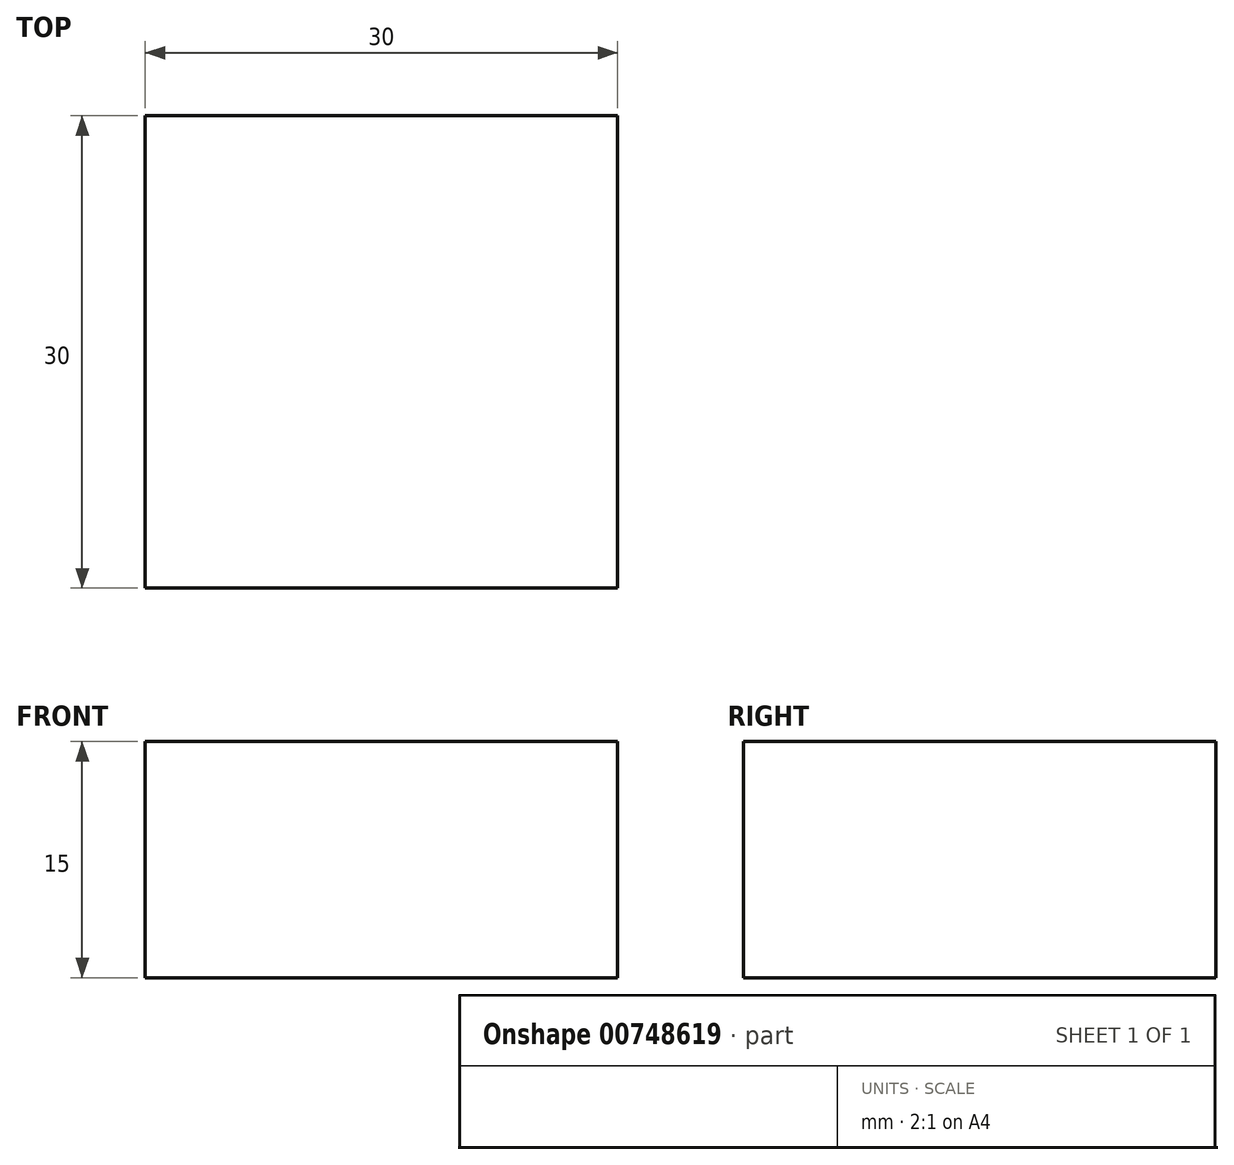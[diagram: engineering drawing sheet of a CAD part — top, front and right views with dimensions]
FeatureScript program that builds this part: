
annotation { "Feature Type Name" : "Feature", "Feature Type Description" : "" }
export const myFeature = defineFeature(function(context is Context, id is Id, definition is map)
    precondition{}
    {
        {
            var Q0;
            Q0=qCreatedBy(makeId("Top.planeOp"),FACE);
            var sketch = newSketch(context, id + "F0", { "sketchPlane" : qUnion([Q0])});
            skLineSegment(sketch, "E0.bottom", {"start": v(-15, -15) * mm, "end": v(15, -15) * mm});
            skLineSegment(sketch, "E0.top", {"start": v(-15, 15) * mm, "end": v(15, 15) * mm});
            skLineSegment(sketch, "E0.left", {"start": v(-15, -15) * mm, "end": v(-15, 15) * mm});
            skLineSegment(sketch, "E0.right", {"start": v(15, -15) * mm, "end": v(15, 15) * mm});
            skPoint(sketch, "E0.middle", {"position": v(0, 0) * mm});
            skSolve(sketch);
        }
        {
            var Q0;
            Q0=makeQuery(id+"F0.imprint","IMPRINT",FACE,{"disambiguationData":[TD([[makeQuery(id+"F0.imprint","IMPRINT",EDGE,{"derivedFrom":sQuery(id+"F0.wireOp",EDGE,"E0.bottom")}),1.0]])]});
            extrude(context, id + "F1", {"entities" : qUnion([Q0]), "depth" : 15 * mm, "offsetDistance" : 25 * mm});
        }
        {
            var Q0;
            Q0=makeQuery(id+"F1.opExtrude","SWEPT_BODY",BODY,{"disambiguationData":[OSD([sQuery(id+"F0.wireOp",EDGE,"E0.bottom"),sQuery(id+"F0.wireOp",EDGE,"E0.top"),sQuery(id+"F0.wireOp",EDGE,"E0.left"),sQuery(id+"F0.wireOp",EDGE,"E0.right")])]});
            transform(context, id + "F2", {"entities" : qUnion([Q0]), "transformType" : TransformType.TRANSLATION_3D, "dx" : 0 * mm, "dy" : 0 * mm, "dz" : 0 * mm, "makeCopy" : true});
        }
    });
